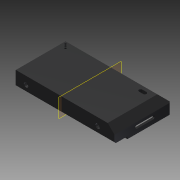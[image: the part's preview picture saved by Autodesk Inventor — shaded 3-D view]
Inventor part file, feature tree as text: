
AUTODESK INVENTOR PART (.ipt)
format: ipt  version: 2015 (Build 190159000, 159)  size: 479,744 bytes
history: native  units: mm
features: extrude x20, fillet x12, other x8, chamfer x5, hole x5, projected_geometry x2, shell x1, plane x1
ambient origin geometry x8: Origin, YZ Plane, XZ Plane, XY Plane, X Axis, Y Axis, Z Axis, Center Point
bodies: Solid1 (feature_tree)
feature tree (54):
  extrude  "Extrusión1"  Depth=155.0mm
  chamfer  "Chaflán11"  Distance=83.0mm
  extrude  "Extrusión39"  Depth=5.0mm
  chamfer  "Chaflán13"  Distance=145.0mm
  hole  "Agujero6"  [1 undecoded]
  extrude  "Extrusión40"  Depth=5.0mm
  fillet  "Empalme35"  Radius=25.0mm
  hole  "Agujero7"  [1 undecoded]
  extrude  "Extrusión41"  Depth=10.0mm
  extrude  "Extrusión42"  Depth=5.0mm
  fillet  "Empalme36"  Radius=5.0mm
  extrude  "Extrusión43"  Depth=1.2mm
  chamfer  "Chaflán14"  Distance=145.0mm
  extrude  "Extrusión44"  Depth=50.0mm
  extrude  "Extrusión45"  Depth=6.0mm
  extrude  "Extrusión46"  Depth=10.0mm TaperAngle=45.0deg
  fillet  "Empalme37"  Radius=10.0mm
  chamfer  "Chaflán15"  Distance=47.9mm
  extrude  "Extrusión47"  Depth=80.0mm
  extrude  "Extrusión48"  Depth=13.5mm
  hole  "Agujero10"  [1 undecoded]
  shell  "Vaciado2"  Thickness=15.0mm
  extrude  "Extrusión21"  Depth=1.2mm
  hole  "Agujero4"  [1 undecoded]
  other  "Desplazar cara15"
  other  "Desplazar cara16"
  other  "Desplazar cara17"
  other  "Desplazar cara19"
  extrude  "Extrusión22"  Depth=1.2mm
  hole  "Agujero5"  [1 undecoded]
  fillet  "Empalme18"  Radius=1.2mm
  extrude  "Extrusión27"  Depth=1.2mm
  fillet  "Empalme19"  Radius=1.2mm
  extrude  "Extrusión28"  Depth=12.0mm
  other  "Desplazar cara20"
  chamfer  "Chaflán12"  Distance=2.0mm
  extrude  "Extrusión30"  Depth=12.5mm TaperAngle=0.0deg
  extrude  "Extrusión31"  Depth=4.0mm
  fillet  "Empalme32"  Radius=30.0mm
  extrude  "Extrusión34"  Depth=4.0mm TaperAngle=0.0deg
  plane  "Plano de trabajo5"
  extrude  "Extrusión36"  Depth=2.0mm
  fillet  "Empalme33"  Radius=2.0mm
  fillet  "Empalme34"  Radius=17.5mm
  extrude  "Extrusión37"  Depth=10.0mm
  fillet  "Empalme25"  Radius=4.0mm
  fillet  "Empalme26"  Radius=2.0mm
  fillet  "Empalme27"  Radius=4.0mm
  fillet  "Empalme23"  Radius=2.0mm
  other  "Desplazar cara12"
  other  "Desplazar cara13"
  other  "Desplazar cara14"
  projected_geometry  "Contorno proyectado8"
  projected_geometry  "Contorno proyectado9"
note: 5 required parameter values undecoded (feature->parameter linkage not recoverable at this tier; creation-order binding heuristic only, values carry confidence <= 0.55)
